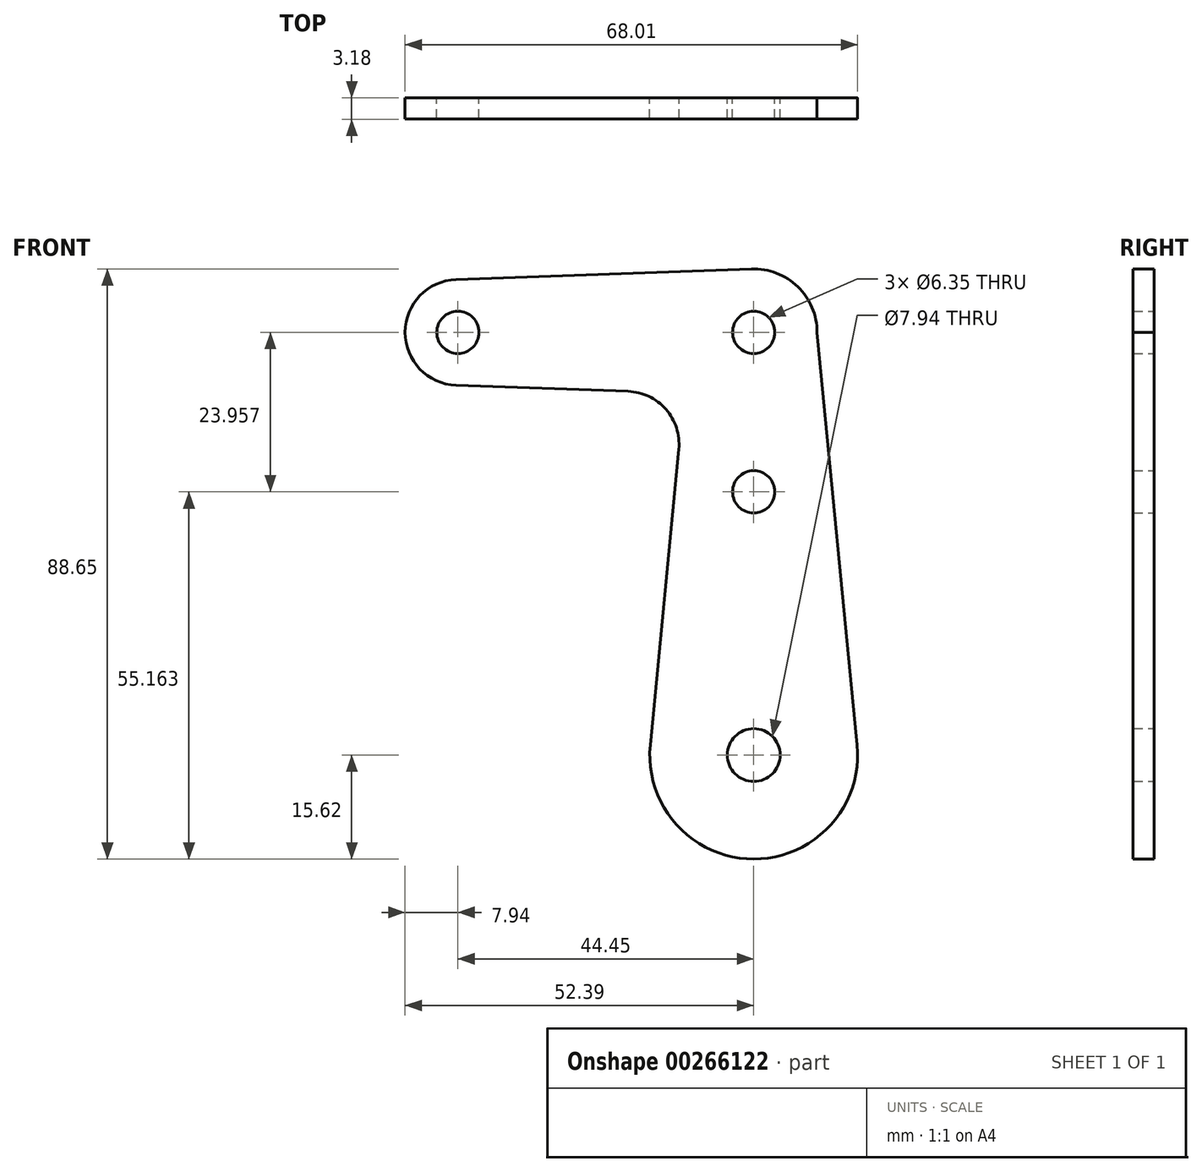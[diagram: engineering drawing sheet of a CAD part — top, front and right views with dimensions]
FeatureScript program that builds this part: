
annotation { "Feature Type Name" : "Feature", "Feature Type Description" : "" }
export const myFeature = defineFeature(function(context is Context, id is Id, definition is map)
    precondition{}
    {
        {
            var Q0;
            Q0=qCreatedBy(makeId("Front.planeOp"),FACE);
            var sketch = newSketch(context, id + "F0", { "sketchPlane" : qUnion([Q0])});
            skLineSegment(sketch, "E0", {"start": v(0, 182.14) * mm, "end": v(0, -307.24) * mm, "construction": true});
            skLineSegment(sketch, "E1", {"start": v(-235.46, 0) * mm, "end": v(270.04, 0) * mm, "construction": true});
            skCircle(sketch, "E2", {"center": v(0, 0) * mm, "radius": 9.53 * mm});
            skCircle(sketch, "E3", {"center": v(0, -63.5) * mm, "radius": 15.62 * mm});
            skCircle(sketch, "E4", {"center": v(-44.45, 0) * mm, "radius": 7.94 * mm});
            skCircle(sketch, "E5", {"center": v(0, 0) * mm, "radius": 3.18 * mm});
            skCircle(sketch, "E6", {"center": v(-44.45, 0) * mm, "radius": 3.18 * mm});
            skCircle(sketch, "E7", {"center": v(0, -63.5) * mm, "radius": 3.97 * mm});
            skLineSegment(sketch, "E8", {"start": v(-52.76, 7.65) * mm, "end": v(0, 9.53) * mm});
            skLineSegment(sketch, "E9", {"start": v(-50, -7.74) * mm, "end": v(10.49, -9.9) * mm});
            skLineSegment(sketch, "E10", {"start": v(17.3, -80.06) * mm, "end": v(9.52, 0) * mm});
            skLineSegment(sketch, "E11", {"start": v(-17.35, -80.64) * mm, "end": v(-8.68, 9.22) * mm});
            skCircle(sketch, "E12", {"center": v(0, -23.96) * mm, "radius": 3.18 * mm});
            skSolve(sketch);
        }
        {
            var Q0;
            Q0 = qSketchRegion(id + "F0", true);
            extrude(context, id + "F1", {"entities" : qUnion([Q0]), "depth" : 3.17 * mm});
        }
        {
            var Q0;
            Q0=makeQuery(id+"F1.opExtrude","SWEPT_EDGE",EDGE,{"disambiguationData":[OSD([sQuery(id+"F0.wireOp",EDGE,"E9"),sQuery(id+"F0.wireOp",EDGE,"E11")])]});
            fillet(context, id + "F2", {"entities" : qUnion([Q0]), "radius" : 7.94 * mm, "tangentPropagation" : true, "allowEdgeOverflow" : false});
        }
    });
